# Revit family: LamiluxLichtkuppelF100_BIM-Revit
name_source: partatom
category: Fenster
revit_build: Autodesk Revit Architecture 2016 (Build: 20150220_1215(x64)
units: mm (PartAtom-declared; Revit-internal decimal feet)

## family parameters
Arbeitsebenenbasiert = Nein
Basisbauteil = Dach
Beim Laden mit Abzugskörper schneiden = Nein
Gemeinsam genutzt = Nein
Immer vertikal = Nein
OmniClass-Nummer = 23.30.30.17.21
OmniClass-Titel = Ridge Metal-Framed Skylights
Raumberechnungspunkt = Nein

## types (78) — shared parameters
Analytische Konstruktion = <None>
BIMobject category = Roof Window
Depth = 0.00
Design country = Germany
Edition number = 1
Hersteller = Lamilux
IFC Classification = Window
Manufacturer country = Germany
Manufacturer name = LAMILUX
Material main = Lamilux-White
Material secondary = Lamilux- Plastic
NBS Reference Code = 20-30-72
NBS Reference Description = Roof Light And Smoke Ventilator Systems
Nominal height = 0.00
Nominal width = 0.00
Product SKU = Lamilux_F100_rooflight_dome
Product family = Daylight element, SHEV
Product group = Rooflight dome
QR code = http://lamilux.bimobject.com
UNSPSC Code = 301516
URL = http://lamilux.bimobject.com
Uniclass 1.4 Code = JL11
Uniclass 1.4 Description = Rooflights/Roof windows
Uniclass 2.0 Code = SS-65-10-80-80
Uniclass 2.0 Description = Smoke And Heat Exhaust Ventilation Systems
Weight Net (Kg) = 0

## per-type parameters (varying)
| type | AW-Wert | CatValue_Height | CatValue_Kerb Height | CatValue_Width |
| 1000X1000X300 | 0.75m² | 1000 mm  [stored 3.28084 ft] | 300 mm | 1000 mm  [stored 3.28084 ft] |
| 2000X2000X500 | 3.00m² | 2000 mm  [stored 6.56168 ft] | 500 mm  [stored 1.64042 ft] | 2000 mm  [stored 6.56168 ft] |
| 2000X2000X400 | 3.00m² | 2000 mm  [stored 6.56168 ft] | 400 mm  [stored 1.31234 ft] | 2000 mm  [stored 6.56168 ft] |
| 2000X2000X300 | 3.00m² | 2000 mm  [stored 6.56168 ft] | 300 mm | 2000 mm  [stored 6.56168 ft] |
| 1800X3000X500 | 4.05m² | 3000 mm  [stored 9.84252 ft] | 500 mm  [stored 1.64042 ft] | 1800 mm  [stored 5.90551 ft] |
| 1800X3000X400 | 4.05m² | 3000 mm  [stored 9.84252 ft] | 400 mm  [stored 1.31234 ft] | 1800 mm  [stored 5.90551 ft] |
| 1800X3000X300 | 4.05m² | 3000 mm  [stored 9.84252 ft] | 300 mm | 1800 mm  [stored 5.90551 ft] |
| 1800X2700X500 | 3.65m² | 2700 mm  [stored 8.85827 ft] | 500 mm  [stored 1.64042 ft] | 1800 mm  [stored 5.90551 ft] |
| 1800X2700X400 | 3.65m² | 2700 mm  [stored 8.85827 ft] | 400 mm  [stored 1.31234 ft] | 1800 mm  [stored 5.90551 ft] |
| 1800X2700X300 | 3.65m² | 2700 mm  [stored 8.85827 ft] | 300 mm | 1800 mm  [stored 5.90551 ft] |
| 1800X2500X500 | 3.38m² | 2500 mm  [stored 8.2021 ft] | 500 mm  [stored 1.64042 ft] | 1800 mm  [stored 5.90551 ft] |
| 1800X2500X400 | 3.38m² | 2500 mm  [stored 8.2021 ft] | 400 mm  [stored 1.31234 ft] | 1800 mm  [stored 5.90551 ft] |
| 1800X2500X300 | 3.38m² | 2500 mm  [stored 8.2021 ft] | 300 mm | 1800 mm  [stored 5.90551 ft] |
| 1800X2400X500 | 3.24m² | 2400 mm | 500 mm  [stored 1.64042 ft] | 1800 mm  [stored 5.90551 ft] |
| 1800X2400X400 | 3.24m² | 2400 mm | 400 mm  [stored 1.31234 ft] | 1800 mm  [stored 5.90551 ft] |
| 1800X2400X300 | 3.24m² | 2400 mm | 300 mm | 1800 mm  [stored 5.90551 ft] |
| 1800X1800X500 | 2.43m² | 1800 mm  [stored 5.90551 ft] | 500 mm  [stored 1.64042 ft] | 1800 mm  [stored 5.90551 ft] |
| 1800X1800X400 | 2.43m² | 1800 mm  [stored 5.90551 ft] | 400 mm  [stored 1.31234 ft] | 1800 mm  [stored 5.90551 ft] |
| 1800X1800X300 | 2.43m² | 1800 mm  [stored 5.90551 ft] | 300 mm | 1800 mm  [stored 5.90551 ft] |
| 1500X3000X500 | 3.38m² | 3000 mm  [stored 9.84252 ft] | 500 mm  [stored 1.64042 ft] | 1500 mm  [stored 4.92126 ft] |
| 1500X3000X400 | 3.38m² | 3000 mm  [stored 9.84252 ft] | 400 mm  [stored 1.31234 ft] | 1500 mm  [stored 4.92126 ft] |
| 1500X3000X300 | 3.38m² | 3000 mm  [stored 9.84252 ft] | 300 mm | 1500 mm  [stored 4.92126 ft] |
| 1500X2500X500 | 2.81m² | 2500 mm  [stored 8.2021 ft] | 500 mm  [stored 1.64042 ft] | 1500 mm  [stored 4.92126 ft] |
| 1500X2500X400 | 2.81m² | 2500 mm  [stored 8.2021 ft] | 400 mm  [stored 1.31234 ft] | 1500 mm  [stored 4.92126 ft] |
| 1500X2500X300 | 2.81m² | 2500 mm  [stored 8.2021 ft] | 300 mm | 1500 mm  [stored 4.92126 ft] |
| 1500X2400X500 | 2.70m² | 2400 mm | 500 mm  [stored 1.64042 ft] | 1500 mm  [stored 4.92126 ft] |
| 1500X2400X400 | 2.70m² | 2400 mm | 400 mm  [stored 1.31234 ft] | 1500 mm  [stored 4.92126 ft] |
| 1500X2400X300 | 2.70m² | 2400 mm | 300 mm | 1500 mm  [stored 4.92126 ft] |
| 1500X2100X500 | 2.36m² | 2100 mm | 500 mm  [stored 1.64042 ft] | 1500 mm  [stored 4.92126 ft] |
| 1500X2100X400 | 2.36m² | 2100 mm | 400 mm  [stored 1.31234 ft] | 1500 mm  [stored 4.92126 ft] |
| 1500X2100X300 | 2.36m² | 2100 mm | 300 mm | 1500 mm  [stored 4.92126 ft] |
| 1500X2000X500 | 2.25m² | 2000 mm  [stored 6.56168 ft] | 500 mm  [stored 1.64042 ft] | 1500 mm  [stored 4.92126 ft] |
| 1500X2000X400 | 2.25m² | 2000 mm  [stored 6.56168 ft] | 400 mm  [stored 1.31234 ft] | 1500 mm  [stored 4.92126 ft] |
| 1500X2000X300 | 2.25m² | 2000 mm  [stored 6.56168 ft] | 300 mm | 1500 mm  [stored 4.92126 ft] |
| 1500X1800X500 | 2.03m² | 1800 mm  [stored 5.90551 ft] | 500 mm  [stored 1.64042 ft] | 1500 mm  [stored 4.92126 ft] |
| 1500X1800X400 | 2.03m² | 1800 mm  [stored 5.90551 ft] | 400 mm  [stored 1.31234 ft] | 1500 mm  [stored 4.92126 ft] |
| 1500X1800X300 | 2.03m² | 1800 mm  [stored 5.90551 ft] | 300 mm | 1500 mm  [stored 4.92126 ft] |
| 1500X1500X500 | 1.69m² | 1500 mm  [stored 4.92126 ft] | 500 mm  [stored 1.64042 ft] | 1500 mm  [stored 4.92126 ft] |
| 1500X1500X400 | 1.69m² | 1500 mm  [stored 4.92126 ft] | 400 mm  [stored 1.31234 ft] | 1500 mm  [stored 4.92126 ft] |
| 1500X1500X300 | 1.69m² | 1500 mm  [stored 4.92126 ft] | 300 mm | 1500 mm  [stored 4.92126 ft] |
| 1250X2500X500 | 1.17m² | 2500 mm  [stored 8.2021 ft] | 500 mm  [stored 1.64042 ft] | 1250 mm  [stored 4.10105 ft] |
| 1250X2500X400 | 1.17m² | 2500 mm  [stored 8.2021 ft] | 400 mm  [stored 1.31234 ft] | 1250 mm  [stored 4.10105 ft] |
| 1250X2500X300 | 1.17m² | 2500 mm  [stored 8.2021 ft] | 300 mm | 1250 mm  [stored 4.10105 ft] |
| 1250X1250X500 | 1.17m² | 1250 mm  [stored 4.10105 ft] | 500 mm  [stored 1.64042 ft] | 1250 mm  [stored 4.10105 ft] |
| 1250X1250X400 | 1.17m² | 1250 mm  [stored 4.10105 ft] | 400 mm  [stored 1.31234 ft] | 1250 mm  [stored 4.10105 ft] |
| 1250X1250X300 | 1.17m² | 1250 mm  [stored 4.10105 ft] | 300 mm | 1250 mm  [stored 4.10105 ft] |
| 1200X3000X500 | 2.70m² | 3000 mm  [stored 9.84252 ft] | 500 mm  [stored 1.64042 ft] | 1200 mm |
| 1200X3000X400 | 2.70m² | 3000 mm  [stored 9.84252 ft] | 400 mm  [stored 1.31234 ft] | 1200 mm |
| 1200X3000X300 | 2.70m² | 3000 mm  [stored 9.84252 ft] | 300 mm | 1200 mm |
| 1200X2400X500 | 2.16m² | 2400 mm | 500 mm  [stored 1.64042 ft] | 1200 mm |
| 1200X2400X400 | 2.16m² | 2400 mm | 400 mm  [stored 1.31234 ft] | 1200 mm |
| 1200X2400X300 | 2.16m² | 2400 mm | 300 mm | 1200 mm |
| 1200X1800X500 | 1.35m² | 1800 mm  [stored 5.90551 ft] | 500 mm  [stored 1.64042 ft] | 1200 mm |
| 1200X1800X400 | 1.35m² | 1800 mm  [stored 5.90551 ft] | 400 mm  [stored 1.31234 ft] | 1200 mm |
| 1200X1800X300 | 1.35m² | 1800 mm  [stored 5.90551 ft] | 300 mm | 1200 mm |
| 1200X1500X500 | 1.35m² | 1500 mm  [stored 4.92126 ft] | 500 mm  [stored 1.64042 ft] | 1200 mm |
| 1200X1500X400 | 1.35m² | 1500 mm  [stored 4.92126 ft] | 400 mm  [stored 1.31234 ft] | 1200 mm |
| 1200X1500X300 | 1.35m² | 1500 mm  [stored 4.92126 ft] | 300 mm | 1200 mm |
| 1200X1200X500 | 1.08m² | 1200 mm | 500 mm  [stored 1.64042 ft] | 1200 mm |
| 1200X1200X400 | 1.08m² | 1200 mm | 400 mm  [stored 1.31234 ft] | 1200 mm |
| 1200X1200X300 | 1.08m² | 1200 mm | 300 mm | 1200 mm |
| 1000X3000X500 | 2.25m² | 3000 mm  [stored 9.84252 ft] | 500 mm  [stored 1.64042 ft] | 1000 mm  [stored 3.28084 ft] |
| 1000X3000X400 | 2.25m² | 3000 mm  [stored 9.84252 ft] | 400 mm  [stored 1.31234 ft] | 1000 mm  [stored 3.28084 ft] |
| 1000X3000X300 | 2.25m² | 3000 mm  [stored 9.84252 ft] | 300 mm | 1000 mm  [stored 3.28084 ft] |
| 1000X2500X500 | 1.88m² | 2500 mm  [stored 8.2021 ft] | 500 mm  [stored 1.64042 ft] | 1000 mm  [stored 3.28084 ft] |
| 1000X2500X400 | 1.88m² | 2500 mm  [stored 8.2021 ft] | 400 mm  [stored 1.31234 ft] | 1000 mm  [stored 3.28084 ft] |
| 1000X2500X300 | 1.88m² | 2500 mm  [stored 8.2021 ft] | 300 mm | 1000 mm  [stored 3.28084 ft] |
| 1000X2400X500 | 1.80m² | 2400 mm | 500 mm  [stored 1.64042 ft] | 1000 mm  [stored 3.28084 ft] |
| 1000X2400X400 | 1.80m² | 2400 mm | 400 mm  [stored 1.31234 ft] | 1000 mm  [stored 3.28084 ft] |
| 1000X2400X300 | 1.80m² | 2400 mm | 300 mm | 1000 mm  [stored 3.28084 ft] |
| 1000X2000X500 | 1.50m² | 2000 mm  [stored 6.56168 ft] | 500 mm  [stored 1.64042 ft] | 1000 mm  [stored 3.28084 ft] |
| 1000X2000X400 | 1.50m² | 2000 mm  [stored 6.56168 ft] | 400 mm  [stored 1.31234 ft] | 1000 mm  [stored 3.28084 ft] |
| 1000X2000X300 | 1.50m² | 2000 mm  [stored 6.56168 ft] | 300 mm | 1000 mm  [stored 3.28084 ft] |
| 1000X1500X500 | 1.13m² | 1500 mm  [stored 4.92126 ft] | 500 mm  [stored 1.64042 ft] | 1000 mm  [stored 3.28084 ft] |
| 1000X1500X400 | 1.13m² | 1500 mm  [stored 4.92126 ft] | 400 mm  [stored 1.31234 ft] | 1000 mm  [stored 3.28084 ft] |
| 1000X1500X300 | 1.13m² | 1500 mm  [stored 4.92126 ft] | 300 mm | 1000 mm  [stored 3.28084 ft] |
| 1000X1000X500 | 0.75m² | 1000 mm  [stored 3.28084 ft] | 500 mm  [stored 1.64042 ft] | 1000 mm  [stored 3.28084 ft] |
| 1000X1000X400 | 0.75m² | 1000 mm  [stored 3.28084 ft] | 400 mm  [stored 1.31234 ft] | 1000 mm  [stored 3.28084 ft] |

note: [stored X ft] marks values corroborated as IEEE doubles in the binary element streams (Revit-internal decimal feet)

## geometry (parser evidence)
native form markers: Blend x9, Sweep x5
no freeform markers — native parametric forms only
